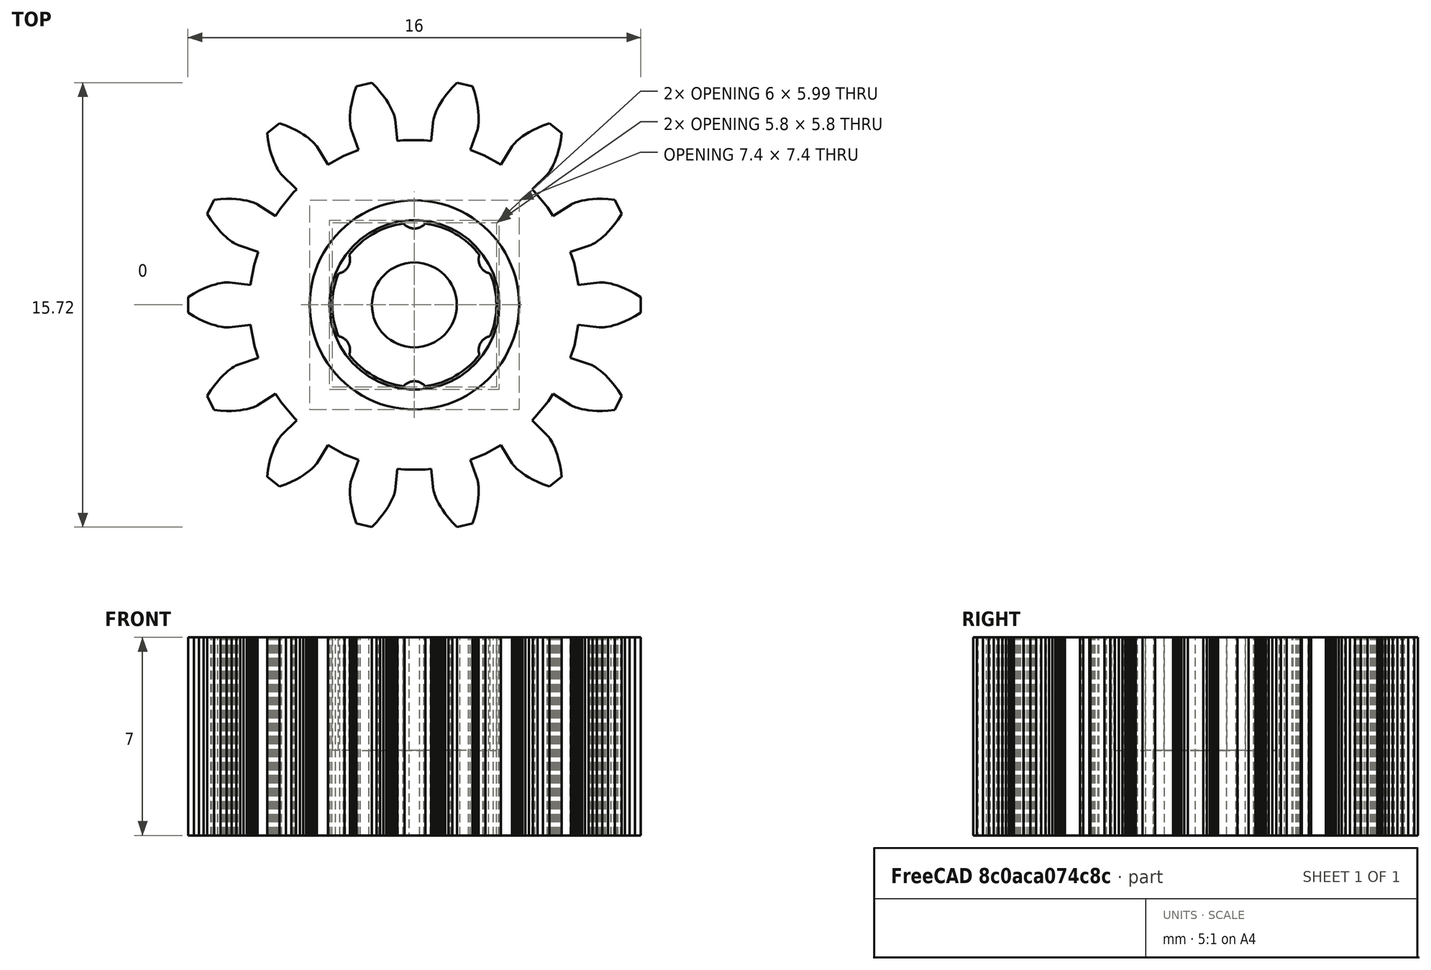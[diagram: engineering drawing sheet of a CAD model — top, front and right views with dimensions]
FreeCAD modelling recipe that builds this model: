
FCSTD DOCUMENT  (FreeCAD 0.19R24291 (Git))
Label: servo_gear_fixation
License: All rights reserved
LicenseURL: http://en.wikipedia.org/wiki/All_rights_reserved
objects: App::FeaturePython×4, Sketcher::SketchObject×2, PartDesign::Pad×2, Part::Feature×2, Part::FeaturePython×2, PartDesign::PolarPattern×1, PartDesign::Body×1, Mesh::Feature×1, Part::Refine×1, Part::Fuse×1
note: 14 computed .brp shape members not serialized (recipe doc carries the construction recipe); baked Part::Feature solids carry a one-line shape summary decoded from their .brp

FEATURE [Sketcher::SketchObject] Sketch  label="adapter_base_sketch"
  FullyConstrained = false
  MapMode = 5
  Support = -> [XY_Plane]
  sketch-geometry (8):
    g0: Circle CenterX=0 CenterY=0 CenterZ=0 NormalX=0 NormalY=0 NormalZ=1 AngleXU=0 Radius=1.5
    g1: Circle CenterX=0 CenterY=0 CenterZ=0 NormalX=0 NormalY=0 NormalZ=1 AngleXU=0 Radius=2.9
    g2: Circle CenterX=0 CenterY=3.2 CenterZ=0 NormalX=0 NormalY=0 NormalZ=1 AngleXU=0 Radius=0.5
    g3: GeomPoint X=0 Y=2.7 Z=0
    g4: GeomPoint X=0 Y=2.9 Z=0
    g5: Circle CenterX=0 CenterY=0 CenterZ=0 NormalX=0 NormalY=0 NormalZ=1 AngleXU=0 Radius=3.7
    g6: ArcOfCircle CenterX=0 CenterY=3.2 CenterZ=0 NormalX=0 NormalY=0 NormalZ=1 AngleXU=0 Radius=0.5 StartAngle=3.84918 EndAngle=5.5756
    g7: ArcOfCircle CenterX=0 CenterY=0 CenterZ=0 NormalX=0 NormalY=0 NormalZ=1 AngleXU=0 Radius=2.9 StartAngle=1.7022 EndAngle=7.72258
  constraints (19):
    c: Coincident(g0,g-1)
    c: Coincident(g1,g0)
    c: PointOnObject(g2,g-2)
    c: Diameter(g2) = 1
    c: Diameter(g0) = 3
    c: Diameter(g1) = 5.8
    c: PointOnObject(g3,g2)
    c: PointOnObject(g4,g1)
    c: PointOnObject(g3,g-2)
    c: PointOnObject(g4,g-2)
    c: DistanceY(g3,g4) = 0.2
    c: Coincident(g5,g0)
    c: Tangent(g5,g2)
    c: Coincident(g6,g2)
    c: PointOnObject(g6,g2)
    c: Coincident(g7,g0)
    c: PointOnObject(g7,g1)
    c: Coincident(g6,g7)
    c: Coincident(g6,g7)
FEATURE [PartDesign::Pad] Pad  label="adapter_base_pad"
  Direction = (1,1,1)
  Length = 7
  Length2 = 100
  Profile = -> Sketch
  Type = 0
FEATURE [Sketcher::SketchObject] Sketch001  label="adapter_lid_sketch"
  ExternalGeometry = -> [Pad]
  FullyConstrained = false
  MapMode = 5
  Support = -> [XY_Plane]
  sketch-geometry (2):
    g0: Circle CenterX=0 CenterY=0 CenterZ=0 NormalX=0 NormalY=0 NormalZ=1 AngleXU=0 Radius=3.7
    g1: Circle CenterX=0 CenterY=0 CenterZ=0 NormalX=0 NormalY=0 NormalZ=1 AngleXU=0 Radius=1.5
  constraints (4):
    c: Coincident(g0,g-1)
    c: Equal(g0,g-3)
    c: Coincident(g1,g0)
    c: Diameter(g1) = 3
FEATURE [PartDesign::PolarPattern] PolarPattern  label="repeat_teeth"
  Angle = 360
  Axis = -> Sketch [N_Axis]
  BaseFeature = -> Pad
  Occurrences = 6
  Originals = -> [Pad]
FEATURE [PartDesign::Pad] Pad001  label="adapter_lid_pad"
  BaseFeature = -> PolarPattern
  Direction = (1,1,1)
  Length = 3
  Length2 = 100
  Profile = -> Sketch001
  Type = 0
FEATURE [PartDesign::Body] Body  label="servo_gear_adapter"
  Group = -> [Sketch,Pad,Sketch001,PolarPattern,Pad001]
  Origin = -> Origin
  Tip = -> Pad001
FEATURE [Mesh::Feature] spur_gear_M1_T14
FEATURE [Part::Feature] spur_gear_M1_T14001
  shape: bbox 15.99 x 15.71 x 7 mm, 2248 faces, 0 solids (baked)
FEATURE [Part::Feature] spur_gear_M1_T14001_solid  label="spur_gear_M1_T14001 (Solid)"
  shape: bbox 15.99 x 15.71 x 7 mm, 2248 faces (baked)
FEATURE [Part::Refine] spur_gear_M1_T14001_solid001  label="spur_gear_refinement"
  Source = -> spur_gear_M1_T14001_solid
FEATURE [Part::FeaturePython] b_servo_gear_fixation_001_  label="servo_gear_fixation_servo_gear_adapter_001"  # a2plus imported part (geometry in sourceFile) (typed FeaturePython)
  a2p_Version = V0.1
  fixedPosition = true
  objectType = a2pPart
  sourceFile = ./../../../../../../../Electronica/robot_pipeteador/pipettin-grbl/models/modelos_XYZS/freecad_pipetting_models/modelos_servo/freecad_base_models/servo_gear_fixation.FCStd
  sourcePart = servo_gear_adapter
  subassemblyImport = false
  timeLastImport = 1.62309e+09
  updateColors = true
FEATURE [Part::FeaturePython] b_servo_gear_fixation_001_001  label="servo_gear_fixation_spur_gear_refinement_001"  # a2plus imported part (geometry in sourceFile) (typed FeaturePython)
  Placement = pos=(3.79525e-07,6.33704e-06,0) rot=(0,0,1;0rad)
  a2p_Version = V0.1
  fixedPosition = false
  objectType = a2pPart
  sourceFile = ./../../../../../../../Electronica/robot_pipeteador/pipettin-grbl/models/modelos_XYZS/freecad_pipetting_models/modelos_servo/freecad_base_models/servo_gear_fixation.FCStd
  sourcePart = spur_gear_refinement
  subassemblyImport = false
  timeLastImport = 1.62309e+09
  updateColors = true
FEATURE [App::FeaturePython] planeCoincident_001  label="planeCoincident_001__servo_gear_fixation_servo_gear_adapter_001"  # a2plus constraint (typed FeaturePython)
  Object1 = b_servo_gear_fixation_001_001
  Object2 = b_servo_gear_fixation_001_
  ParentTreeObject = -> b_servo_gear_fixation_001_001
  SubElement1 = Face3
  SubElement2 = Face9
  Suppressed = false
  Type = plane
  directionConstraint = 1
  offset = 0
FEATURE [App::FeaturePython] planeCoincident_001_mirror  label="planeCoincident_001__servo_gear_fixation_spur_gear_refinement_001"  # a2plus constraint (typed FeaturePython)
  Object1 = b_servo_gear_fixation_001_001
  Object2 = b_servo_gear_fixation_001_
  ParentTreeObject = -> b_servo_gear_fixation_001_
  SubElement1 = Face3
  SubElement2 = Face9
  Suppressed = false
  Type = plane
  directionConstraint = 1
  offset = 0
FEATURE [App::FeaturePython] centerOfMass_001  label="centerOfMass_001__servo_gear_fixation_servo_gear_adapter_001"  # a2plus constraint (typed FeaturePython)
  Object1 = b_servo_gear_fixation_001_001
  Object2 = b_servo_gear_fixation_001_
  ParentTreeObject = -> b_servo_gear_fixation_001_001
  SubElement1 = Face3
  SubElement2 = Face9
  Suppressed = false
  Type = CenterOfMass
  directionConstraint = 1
  lockRotation = false
  offset = 0
FEATURE [App::FeaturePython] centerOfMass_001_mirror  label="centerOfMass_001__servo_gear_fixation_spur_gear_refinement_001"  # a2plus constraint (typed FeaturePython)
  Object1 = b_servo_gear_fixation_001_001
  Object2 = b_servo_gear_fixation_001_
  ParentTreeObject = -> b_servo_gear_fixation_001_
  SubElement1 = Face3
  SubElement2 = Face9
  Suppressed = false
  Type = CenterOfMass
  directionConstraint = 1
  lockRotation = false
  offset = 0
FEATURE [Part::Fuse] Fusion
  Base = -> b_servo_gear_fixation_001_
  Tool = -> b_servo_gear_fixation_001_001
